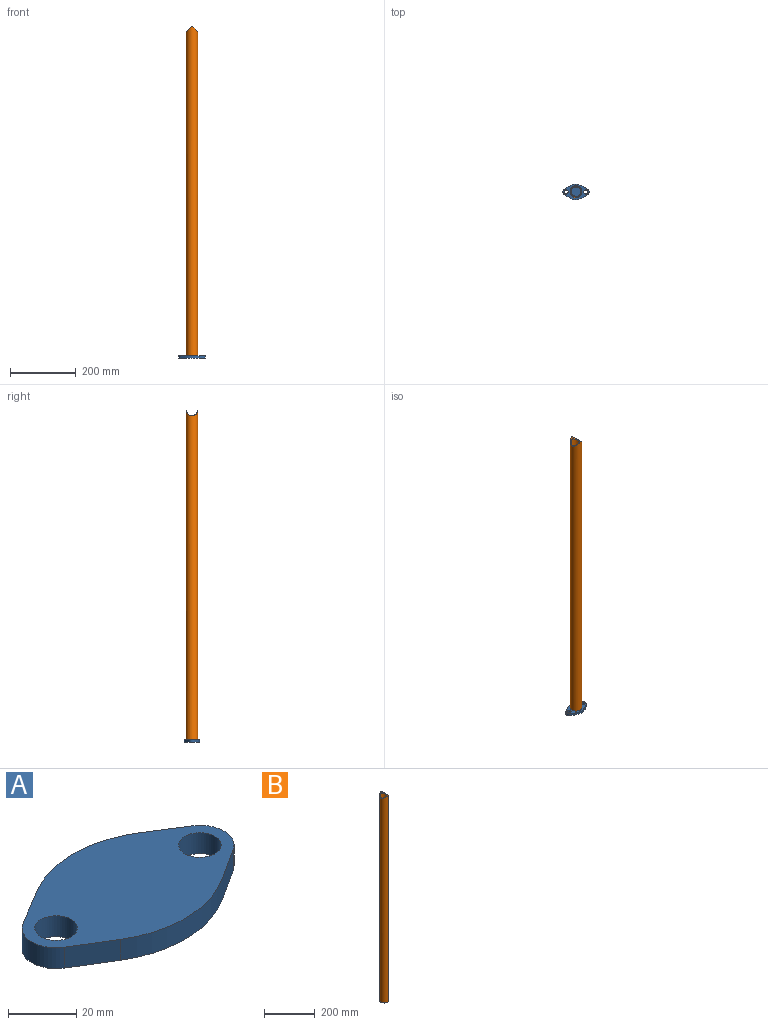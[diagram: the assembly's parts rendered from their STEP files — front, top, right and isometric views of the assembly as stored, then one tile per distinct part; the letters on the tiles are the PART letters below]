
ASSEMBLY  parts=2 mates=1
PART A: 12 faces, bbox 79.7x46.5x7.5 mm
  f0: cylinder r=10.01mm len=16.88mm, axis (0,0,-1), area 150.6mm2, adj f1,f9,f10,f11
  f1: plane 13.51x8.51mm, normal (0.53,0.85,0), area 119.7mm2, adj f0,f2,f10,f11
  f2: cylinder r=40mm len=41.91mm, axis (0,0,-1), area 330.8mm2, adj f1,f3,f10,f11
  f3: plane 14.77x8.86mm, normal (-0.51,0.86,0), area 129.2mm2, adj f2,f4,f10,f11
  f4: cylinder r=10mm len=17.1mm, axis (0,0,-1), area 153.8mm2, adj f3,f5,f10,f11
  f5: plane 14.51x8.9mm, normal (-0.52,-0.85,0), area 127.7mm2, adj f4,f6,f10,f11
  f6: cylinder r=40mm len=42.58mm, axis (0,0,-1), area 336.7mm2, adj f5,f9,f10,f11
  f7: cylinder r=6.25mm len=12.5mm, axis (0,0,-1), area 294.5mm2, adj f10,f11
  f8: cylinder r=6.25mm len=12.5mm, axis (0,0,-1), area 294.5mm2, adj f10,f11
  f9: plane 13.26x8.54mm, normal (0.54,-0.84,0), area 118.3mm2, adj f0,f6,f10,f11
  f10: plane 79.71x46.46mm, normal (0,0,1), area 2386.4mm2, adj f0,f1,f2,f3,f4,f5,f6,f7
  f11: plane 79.71x46.46mm, normal (0,0,-1), area 2386.4mm2, adj f0,f1,f2,f3,f4,f5,f6,f7
PART B: 4 faces, bbox 35.1x35x1000 mm
  f0: cylinder r=15mm len=990.99mm, axis (0,0,-1), area 92966.4mm2, adj f2,f3
  f1: cylinder r=17.5mm len=1000mm, axis (0,0,-1), area 108730.7mm2, adj f2,f3
  f2: plane 35x35mm, normal (0,0,-1), area 255.3mm2, adj f0,f1
  f3: cylinder r=17.5mm len=35.12mm, axis (-1,0,0), area 422.6mm2, adj f0,f1
PLACE A t=(1.03,0.51,0)mm
PLACE B t=(0.28,0.33,7.5)mm
MATE parallel B.f0 <-> A.f10  axis (0,0,-1) through (0.28,0.33,7.5)mm
